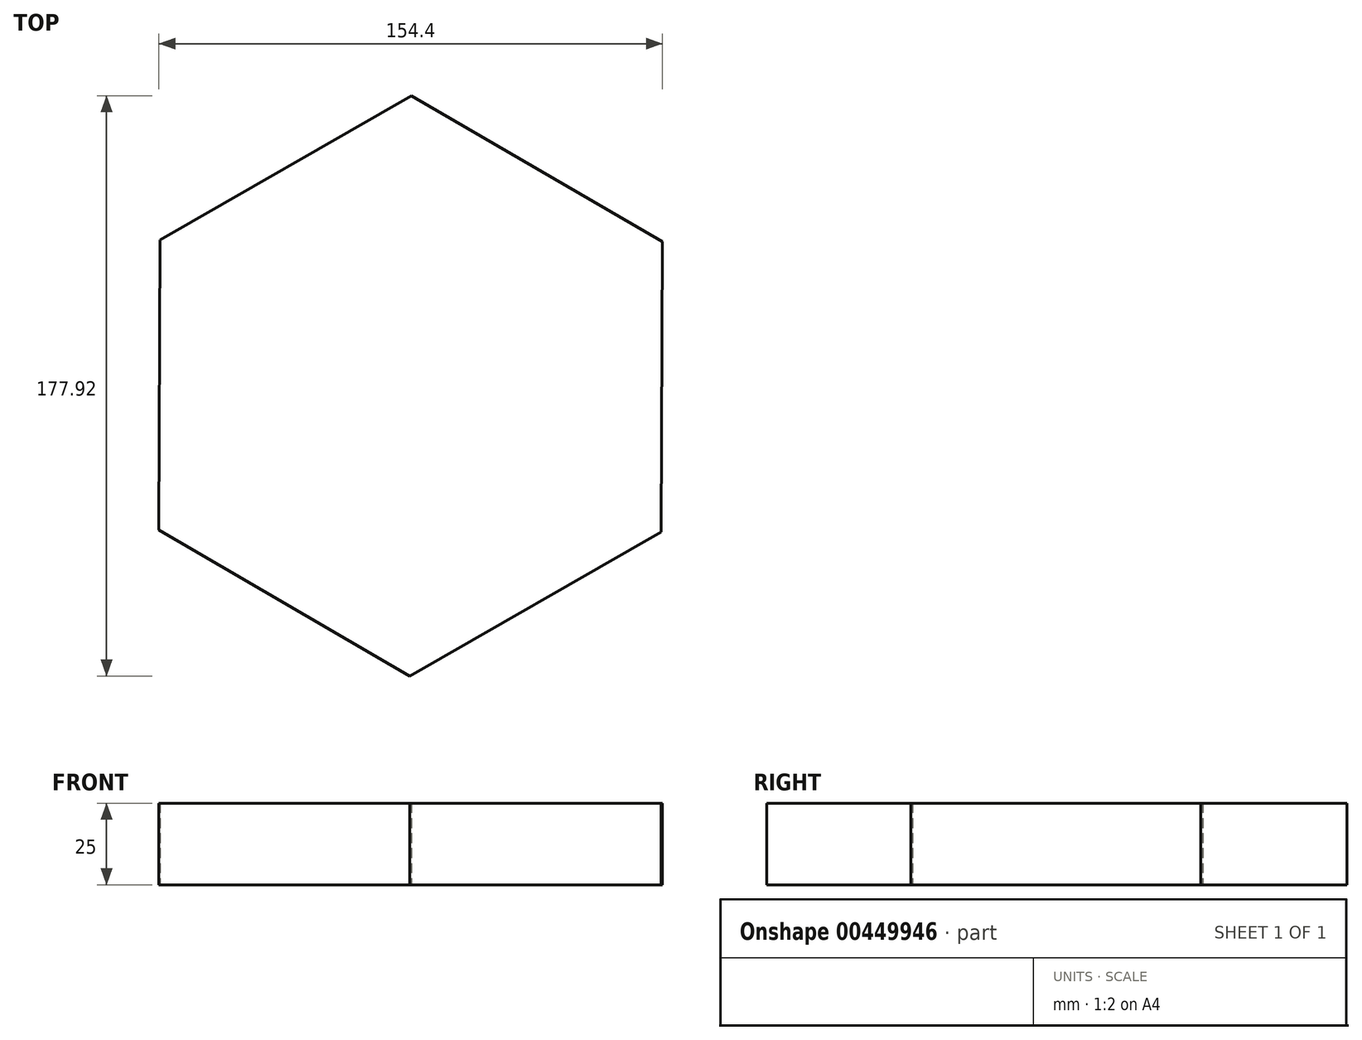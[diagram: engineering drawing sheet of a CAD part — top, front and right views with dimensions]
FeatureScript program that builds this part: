
annotation { "Feature Type Name" : "Feature", "Feature Type Description" : "" }
export const myFeature = defineFeature(function(context is Context, id is Id, definition is map)
    precondition{}
    {
        {
            var Q0;
            Q0=qCreatedBy(makeId("Top.planeOp"),FACE);
            var sketch = newSketch(context, id + "F0", { "sketchPlane" : qUnion([Q0])});
            skCircle(sketch, "E0.cCircle", {"center": v(0, 0) * mm, "radius": 77.04 * mm, "construction": true});
            skLineSegment(sketch, "E0.0", {"start": v(0.31, 88.96) * mm, "end": v(77.2, 44.2) * mm});
            skLineSegment(sketch, "E0.1", {"start": v(77.2, 44.2) * mm, "end": v(76.88, -44.75) * mm});
            skLineSegment(sketch, "E0.2", {"start": v(76.88, -44.75) * mm, "end": v(-0.31, -88.96) * mm});
            skLineSegment(sketch, "E0.3", {"start": v(-0.31, -88.96) * mm, "end": v(-77.2, -44.2) * mm});
            skLineSegment(sketch, "E0.4", {"start": v(-77.2, -44.2) * mm, "end": v(-76.88, 44.75) * mm});
            skLineSegment(sketch, "E0.5", {"start": v(-76.88, 44.75) * mm, "end": v(0.31, 88.96) * mm});
            skPoint(sketch, "E0.0.midPoint", {"position": v(38.75, 66.58) * mm});
            skSolve(sketch);
        }
        {
            var Q0;
            Q0=makeQuery(id+"F0.imprint","IMPRINT",FACE,{"disambiguationData":[TD([[makeQuery(id+"F0.imprint","IMPRINT",EDGE,{"derivedFrom":sQuery(id+"F0.wireOp",EDGE,"E0.0")}),-1.0]])]});
            extrude(context, id + "F1", {"entities" : qUnion([Q0]), "depth" : 25 * mm});
        }
    });
